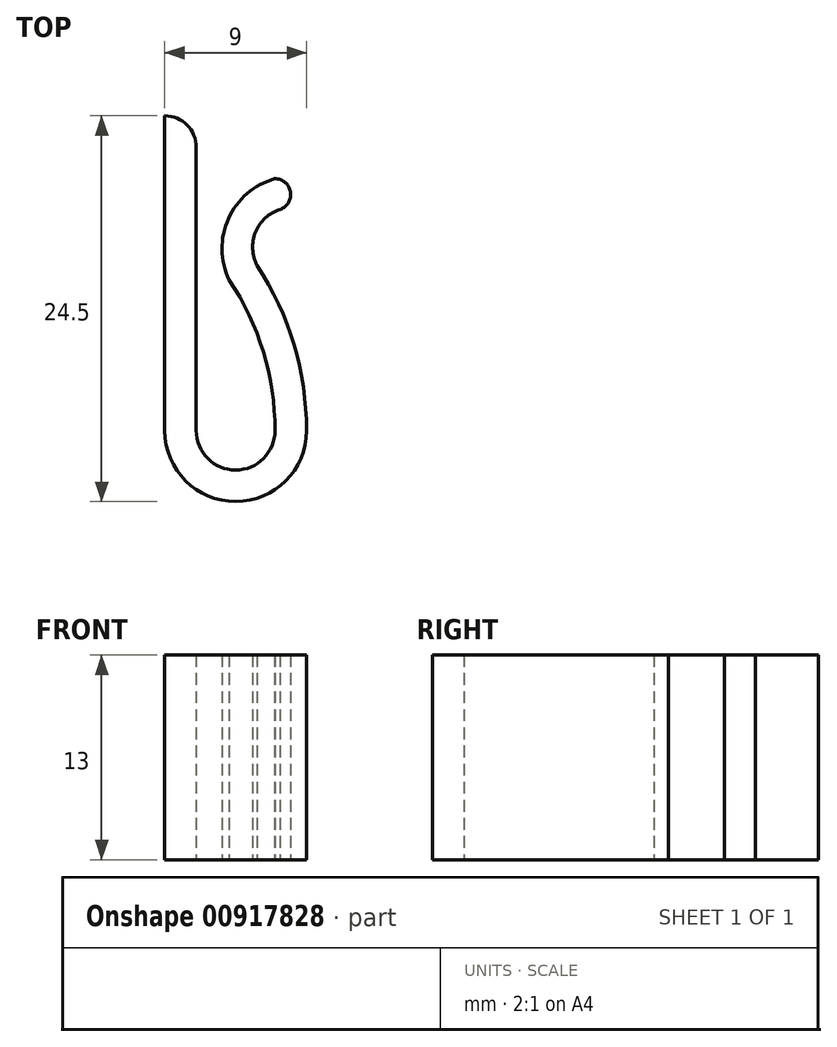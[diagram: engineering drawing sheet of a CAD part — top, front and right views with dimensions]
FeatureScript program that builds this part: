
annotation { "Feature Type Name" : "Feature", "Feature Type Description" : "" }
export const myFeature = defineFeature(function(context is Context, id is Id, definition is map)
    precondition{}
    {
        {
            var Q0;
            Q0=qCreatedBy(makeId("Top.planeOp"),FACE);
            var sketch = newSketch(context, id + "F0", { "sketchPlane" : qUnion([Q0])});
            skLineSegment(sketch, "E0.top", {"start": v(0, 24.5) * mm, "end": v(-2, 24.5) * mm});
            skLineSegment(sketch, "E0.right", {"start": v(-2, 4.5) * mm, "end": v(-2, 24.5) * mm});
            skArc(sketch, "E1", {"start": v(0, 4.5) * mm, "mid": v(2.5, 2) * mm, "end": v(5, 4.5) * mm});
            skArc(sketch, "E2.trimOffspring", {"start": v(-2, 4.5) * mm, "mid": v(2.5, 0) * mm, "end": v(7, 4.5) * mm});
            skLineSegment(sketch, "E3.trimOffspring", {"start": v(0, 4.5) * mm, "end": v(0, 10) * mm});
            skLineSegment(sketch, "E4.trimOffspring", {"start": v(0, 4.5) * mm, "end": v(0, 24.5) * mm});
            skPoint(sketch, "E5.right.start.orphan", {"position": v(5, 0) * mm});
            skLineSegment(sketch, "E6", {"start": v(-2, 4.5) * mm, "end": v(12.24, 4.5) * mm, "construction": true});
            skLineSegment(sketch, "E7", {"start": v(-7.5, 14.5) * mm, "end": v(17.5, 14.5) * mm, "construction": true});
            skArc(sketch, "E8", {"start": v(2, 14.5) * mm, "mid": v(2.06, 14.15) * mm, "end": v(2.25, 13.84) * mm});
            skLineSegment(sketch, "E9", {"start": v(-7.5, 19.5) * mm, "end": v(17.5, 19.5) * mm, "construction": true});
            skArc(sketch, "E10", {"start": v(5.29, 18.54) * mm, "mid": v(5.89, 19.96) * mm, "end": v(4.38, 20.28) * mm});
            skArc(sketch, "E11", {"start": v(5, 4.5) * mm, "mid": v(4.26, 9.5) * mm, "end": v(2.1, 14.07) * mm});
            skArc(sketch, "E12", {"start": v(7, 4.5) * mm, "mid": v(6.2, 9.97) * mm, "end": v(3.87, 14.99) * mm});
            skArc(sketch, "E13", {"start": v(4.99, 20.5) * mm, "mid": v(2.04, 17.96) * mm, "end": v(2.1, 14.07) * mm});
            skArc(sketch, "E14", {"start": v(5.33, 18.56) * mm, "mid": v(3.76, 17.11) * mm, "end": v(3.87, 14.99) * mm});
            skArc(sketch, "E15.trimOffspring", {"start": v(4, 14.5) * mm, "mid": v(3.97, 14.75) * mm, "end": v(3.87, 14.99) * mm});
            skSolve(sketch);
        }
        {
            var Q0;
            {var subQ5=sQuery(id+"F0.wireOp",EDGE,"E0.top");Q0=makeQuery(id+"F0.imprint","IMPRINT",FACE,{"disambiguationData":[TD([[makeQuery(id+"F0.imprint","IMPRINT",EDGE,{"derivedFrom":subQ5}),1.0]])]});}
            extrude(context, id + "F1", {"entities" : qUnion([Q0]), "depth" : 13 * mm, "offsetDistance" : 25 * mm});
        }
        {
            var Q0;
            Q0=makeQuery(id+"F1.opExtrude","SWEPT_EDGE",EDGE,{"disambiguationData":[OSD([sQuery(id+"F0.wireOp",EDGE,"E0.top"),sQuery(id+"F0.wireOp",EDGE,"E4.trimOffspring")])]});
            fillet(context, id + "F2", {"entities" : qUnion([Q0]), "radius" : 2 * mm, "tangentPropagation" : true, "allowEdgeOverflow" : false});
        }
    });
